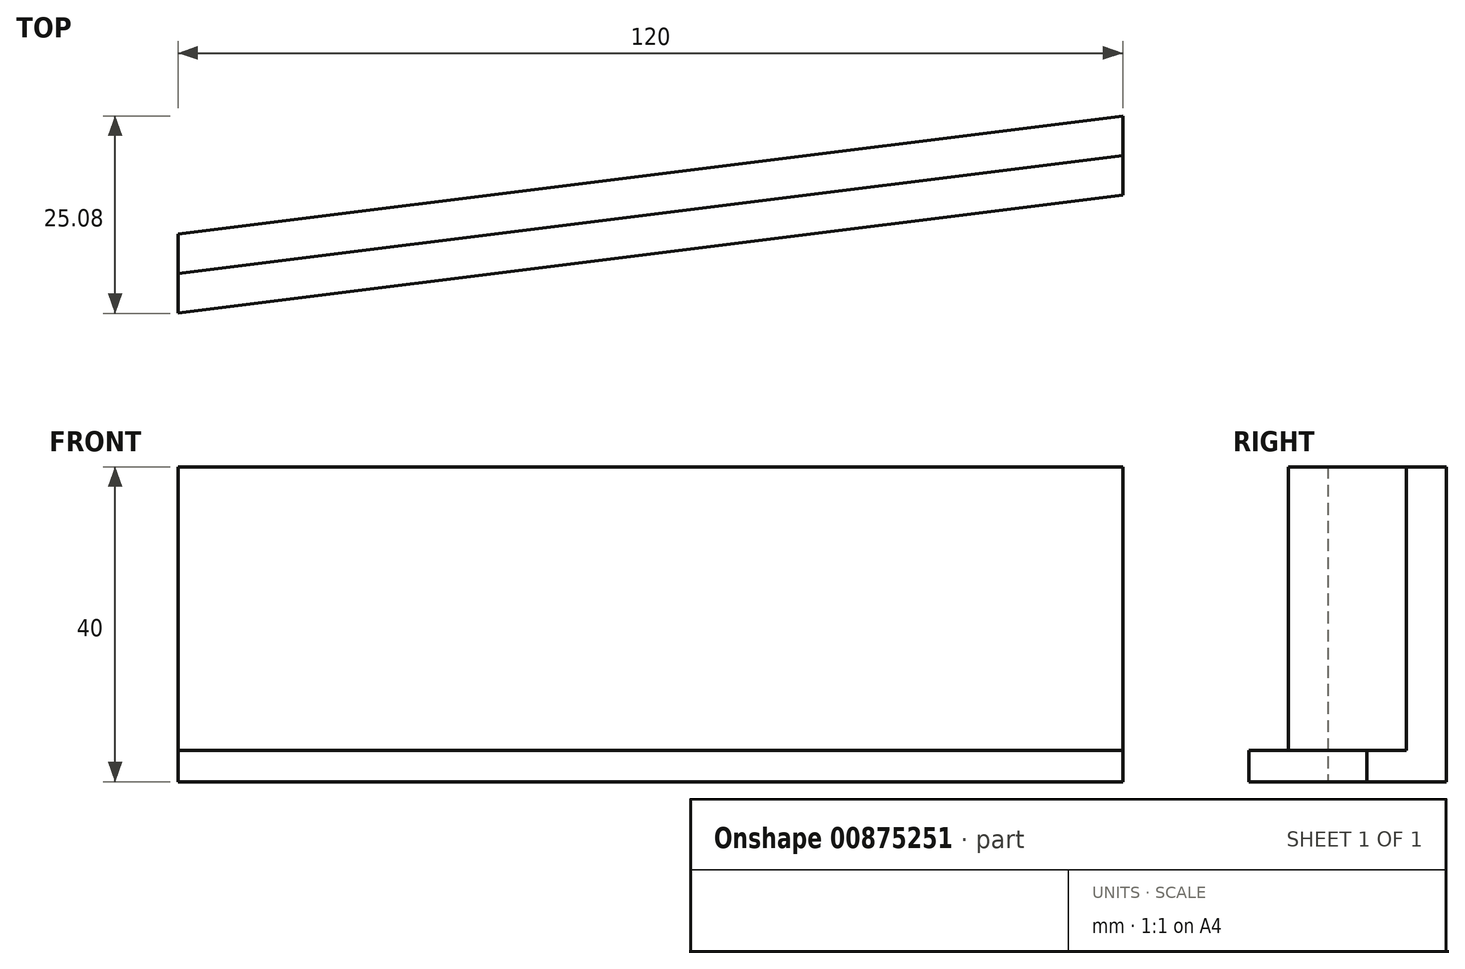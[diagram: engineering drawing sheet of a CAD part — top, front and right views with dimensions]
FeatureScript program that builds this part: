
annotation { "Feature Type Name" : "Feature", "Feature Type Description" : "" }
export const myFeature = defineFeature(function(context is Context, id is Id, definition is map)
    precondition{}
    {
        {
            var Q0;
            Q0=qCreatedBy(makeId("Top.planeOp"),FACE);
            var sketch = newSketch(context, id + "F0", { "sketchPlane" : qUnion([Q0])});
            skLineSegment(sketch, "E0", {"start": v(0, 0) * mm, "end": v(0, -45) * mm, "construction": true});
            skLineSegment(sketch, "E1", {"start": v(0, -45) * mm, "end": v(120, -45) * mm, "construction": true});
            skLineSegment(sketch, "E2", {"start": v(120, -45) * mm, "end": v(120, 15) * mm, "construction": true});
            skLineSegment(sketch, "E3", {"start": v(120, 15) * mm, "end": v(0, 0) * mm});
            skLineSegment(sketch, "E4", {"start": v(0, -5.04) * mm, "end": v(120, 9.96) * mm});
            skLineSegment(sketch, "E5", {"start": v(0, 0) * mm, "end": v(0, -5.04) * mm});
            skLineSegment(sketch, "E6", {"start": v(120, 15) * mm, "end": v(120, 9.96) * mm});
            skSolve(sketch);
        }
        {
            var Q0;
            Q0 = qSketchRegion(id + "F0", true);
            extrude(context, id + "F1", {"entities" : qUnion([Q0]), "depth" : 40 * mm, "offsetDistance" : 25 * mm});
        }
        {
            var Q0;
            Q0=makeQuery(id+"F1.opExtrude","CAP_FACE",FACE,{"disambiguationData":[OSD([sQuery(id+"F0.wireOp",EDGE,"E3"),sQuery(id+"F0.wireOp",EDGE,"E4"),sQuery(id+"F0.wireOp",EDGE,"E5"),sQuery(id+"F0.wireOp",EDGE,"E6")])],"isStart":true});
            var sketch = newSketch(context, id + "F2", { "sketchPlane" : qUnion([Q0])});
            skLineSegment(sketch, "E7.0", {"start": v(0, 5.04) * mm, "end": v(120, -9.96) * mm});
            skLineSegment(sketch, "E8", {"start": v(0, 5.04) * mm, "end": v(0, 10.08) * mm});
            skLineSegment(sketch, "E9", {"start": v(0, 10.08) * mm, "end": v(120, -4.92) * mm});
            skLineSegment(sketch, "E10", {"start": v(120, -4.92) * mm, "end": v(120, -9.96) * mm});
            skSolve(sketch);
        }
        {
            var Q0;
            Q0 = qSketchRegion(id + "F2", true);
            extrude(context, id + "F3", {"entities" : qUnion([Q0]), "operationType" : NewBodyOperationType.ADD, "oppositeDirection" : true, "depth" : 4 * mm, "offsetDistance" : 25 * mm});
        }
    });
